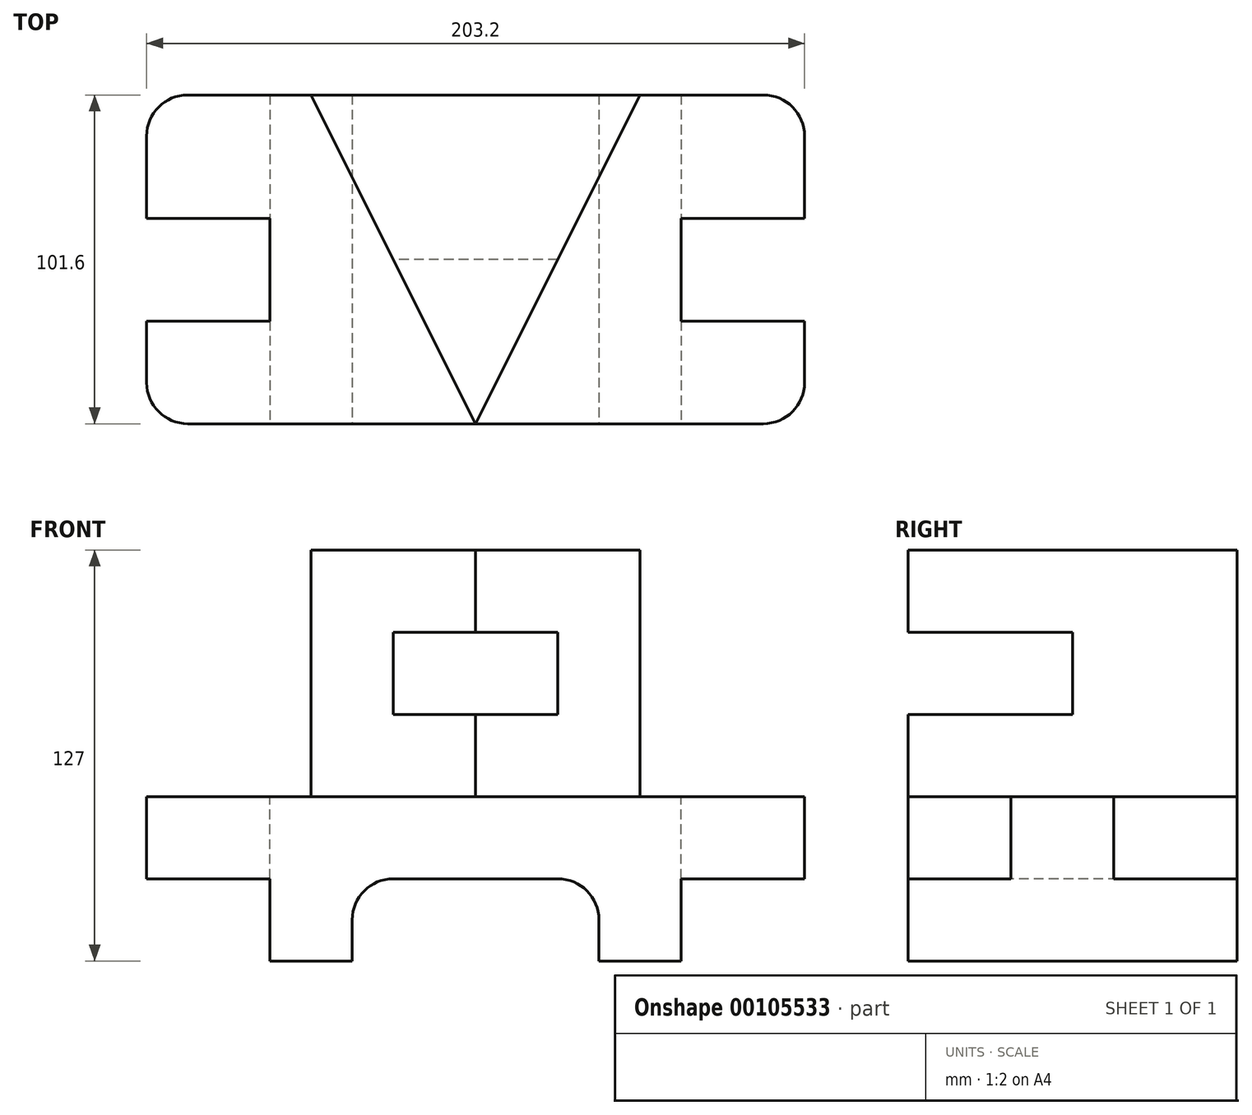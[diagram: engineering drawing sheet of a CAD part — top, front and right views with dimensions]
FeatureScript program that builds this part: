
annotation { "Feature Type Name" : "Feature", "Feature Type Description" : "" }
export const myFeature = defineFeature(function(context is Context, id is Id, definition is map)
    precondition{}
    {
        {
            var Q0;
            Q0=qCreatedBy(makeId("Front.planeOp"),FACE);
            var sketch = newSketch(context, id + "F0", { "sketchPlane" : qUnion([Q0])});
            skLineSegment(sketch, "E0", {"start": v(0, 0) * mm, "end": v(0, 25.4) * mm, "construction": true});
            skLineSegment(sketch, "E1", {"start": v(0, 0) * mm, "end": v(-38.1, 0) * mm, "construction": true});
            skLineSegment(sketch, "E2", {"start": v(-38.1, 0) * mm, "end": v(-38.1, 12.7) * mm});
            skLineSegment(sketch, "E3", {"start": v(0, 25.4) * mm, "end": v(-25.4, 25.4) * mm});
            skArc(sketch, "E4", {"start": v(-25.4, 25.4) * mm, "mid": v(-34.38, 21.68) * mm, "end": v(-38.1, 12.7) * mm});
            skLineSegment(sketch, "E5", {"start": v(-38.1, 0) * mm, "end": v(-63.5, 0) * mm});
            skLineSegment(sketch, "E6", {"start": v(-63.5, 0) * mm, "end": v(-63.5, 25.4) * mm});
            skLineSegment(sketch, "E7", {"start": v(-63.5, 25.4) * mm, "end": v(-101.6, 25.4) * mm});
            skLineSegment(sketch, "E8", {"start": v(-101.6, 25.4) * mm, "end": v(-101.6, 50.8) * mm});
            skLineSegment(sketch, "E9", {"start": v(-101.6, 50.8) * mm, "end": v(0, 50.8) * mm});
            skLineSegment(sketch, "E10.MirrorCS", {"start": v(101.6, 50.8) * mm, "end": v(0, 50.8) * mm});
            skLineSegment(sketch, "E11.MirrorCS", {"start": v(0, 0) * mm, "end": v(38.1, 0) * mm, "construction": true});
            skLineSegment(sketch, "E12.MirrorCS", {"start": v(38.1, 0) * mm, "end": v(38.1, 12.7) * mm});
            skLineSegment(sketch, "E13.MirrorCS", {"start": v(38.1, 0) * mm, "end": v(63.5, 0) * mm});
            skLineSegment(sketch, "E14.MirrorCS", {"start": v(63.5, 25.4) * mm, "end": v(101.6, 25.4) * mm});
            skArc(sketch, "E15.MirrorCS", {"start": v(25.4, 25.4) * mm, "mid": v(34.38, 21.68) * mm, "end": v(38.1, 12.7) * mm});
            skLineSegment(sketch, "E16.MirrorCS", {"start": v(0, 25.4) * mm, "end": v(25.4, 25.4) * mm});
            skLineSegment(sketch, "E17.MirrorCS", {"start": v(63.5, 0) * mm, "end": v(63.5, 25.4) * mm});
            skLineSegment(sketch, "E18.MirrorCS", {"start": v(101.6, 25.4) * mm, "end": v(101.6, 50.8) * mm});
            skSolve(sketch);
        }
        {
            var Q0;
            Q0 = qSketchRegion(id + "F0", true);
            extrude(context, id + "F1", {"entities" : qUnion([Q0]), "oppositeDirection" : true, "depth" : 101.6 * mm});
        }
        {
            var Q0;
            Q0=makeQuery(id+"F1.opExtrude","SWEPT_FACE",FACE,{"disambiguationData":[OSD([sQuery(id+"F0.wireOp",EDGE,"E9"),sQuery(id+"F0.wireOp",EDGE,"E10.MirrorCS")])]});
            var sketch = newSketch(context, id + "F2", { "sketchPlane" : qUnion([Q0])});
            skLineSegment(sketch, "E19", {"start": v(0, 0) * mm, "end": v(-63.5, 0) * mm, "construction": true});
            skLineSegment(sketch, "E20", {"start": v(-63.5, 0) * mm, "end": v(-63.5, 31.75) * mm, "construction": true});
            skLineSegment(sketch, "E21", {"start": v(-63.5, 31.75) * mm, "end": v(-63.5, 63.5) * mm, "construction": true});
            skLineSegment(sketch, "E22", {"start": v(-63.5, 31.75) * mm, "end": v(-101.6, 31.75) * mm});
            skLineSegment(sketch, "E23", {"start": v(-63.5, 31.75) * mm, "end": v(-63.5, 63.5) * mm});
            skLineSegment(sketch, "E24", {"start": v(-63.5, 63.5) * mm, "end": v(-101.6, 63.5) * mm});
            skLineSegment(sketch, "E25", {"start": v(-101.6, 63.5) * mm, "end": v(-101.6, 31.75) * mm});
            skLineSegment(sketch, "E26.MirrorCS", {"start": v(63.5, 31.75) * mm, "end": v(63.5, 63.5) * mm, "construction": true});
            skLineSegment(sketch, "E27.MirrorCS", {"start": v(63.5, 63.5) * mm, "end": v(101.6, 63.5) * mm});
            skLineSegment(sketch, "E28.MirrorCS", {"start": v(63.5, 31.75) * mm, "end": v(101.6, 31.75) * mm});
            skLineSegment(sketch, "E29.MirrorCS", {"start": v(101.6, 63.5) * mm, "end": v(101.6, 31.75) * mm});
            skLineSegment(sketch, "E30", {"start": v(63.5, 63.5) * mm, "end": v(63.5, 31.75) * mm});
            skSolve(sketch);
        }
        {
            var Q0;
            Q0=makeQuery(id+"F2.imprint","IMPRINT",FACE,{"disambiguationData":[TD([[makeQuery(id+"F2.imprint","IMPRINT",EDGE,{"derivedFrom":sQuery(id+"F2.wireOp",EDGE,"E27.MirrorCS")}),-1.0]])]});
            var Q1;
            Q1=makeQuery(id+"F2.imprint","IMPRINT",FACE,{"disambiguationData":[TD([[makeQuery(id+"F2.imprint","IMPRINT",EDGE,{"derivedFrom":sQuery(id+"F2.wireOp",EDGE,"E22")}),-1.0]])]});
            extrude(context, id + "F3", {"entities" : qUnion([Q0, Q1]), "operationType" : NewBodyOperationType.REMOVE, "oppositeDirection" : true, "depth" : 25.4 * mm});
        }
        {
            var Q0;
            Q0=makeQuery(id+"F1.opExtrude","SWEPT_FACE",FACE,{"disambiguationData":[OSD([sQuery(id+"F0.wireOp",EDGE,"E9"),sQuery(id+"F0.wireOp",EDGE,"E10.MirrorCS")])]});
            var sketch = newSketch(context, id + "F4", { "sketchPlane" : qUnion([Q0])});
            skLineSegment(sketch, "E31", {"start": v(0, 0) * mm, "end": v(0, 101.6) * mm, "construction": true});
            skLineSegment(sketch, "E32", {"start": v(0, 101.6) * mm, "end": v(-50.8, 101.6) * mm, "construction": true});
            skLineSegment(sketch, "E33", {"start": v(0, 101.6) * mm, "end": v(50.8, 101.6) * mm, "construction": true});
            skLineSegment(sketch, "E34", {"start": v(-50.8, 101.6) * mm, "end": v(50.8, 101.6) * mm});
            skLineSegment(sketch, "E35", {"start": v(-50.8, 101.6) * mm, "end": v(0, 0) * mm});
            skLineSegment(sketch, "E36", {"start": v(0, 0) * mm, "end": v(50.8, 101.6) * mm});
            skSolve(sketch);
        }
        {
            var Q0;
            Q0 = qSketchRegion(id + "F4", true);
            extrude(context, id + "F5", {"entities" : qUnion([Q0]), "operationType" : NewBodyOperationType.ADD, "depth" : 76.2 * mm});
        }
        {
            var Q0;
            Q0=qCreatedBy(makeId("Front.planeOp"),FACE);
            var sketch = newSketch(context, id + "F6", { "sketchPlane" : qUnion([Q0])});
            skLineSegment(sketch, "E37", {"start": v(0, 0) * mm, "end": v(0, 76.2) * mm, "construction": true});
            skLineSegment(sketch, "E38", {"start": v(0, 76.2) * mm, "end": v(-50.8, 76.2) * mm});
            skLineSegment(sketch, "E39", {"start": v(-50.8, 76.2) * mm, "end": v(-50.8, 101.6) * mm});
            skLineSegment(sketch, "E40", {"start": v(0, 76.2) * mm, "end": v(50.8, 76.2) * mm});
            skLineSegment(sketch, "E41", {"start": v(50.8, 76.2) * mm, "end": v(50.8, 101.6) * mm});
            skLineSegment(sketch, "E42", {"start": v(50.8, 101.6) * mm, "end": v(-50.8, 101.6) * mm});
            skSolve(sketch);
        }
        {
            var Q0;
            Q0=makeQuery(id+"F6.imprint","IMPRINT",FACE,{"disambiguationData":[TD([[makeQuery(id+"F6.imprint","IMPRINT",EDGE,{"derivedFrom":sQuery(id+"F6.wireOp",EDGE,"E38")}),-1.0]])]});
            extrude(context, id + "F7", {"entities" : qUnion([Q0]), "operationType" : NewBodyOperationType.REMOVE, "oppositeDirection" : true, "depth" : 50.8 * mm});
        }
        {
            var Q0;
            Q0=qCreatedBy(makeId("Top.planeOp"),FACE);
            var sketch = newSketch(context, id + "F8", { "sketchPlane" : qUnion([Q0])});
            skLineSegment(sketch, "E43", {"start": v(0, 0) * mm, "end": v(-88.9, 0) * mm, "construction": true});
            skLineSegment(sketch, "E44", {"start": v(-88.9, 0) * mm, "end": v(-88.9, 12.7) * mm, "construction": true});
            skLineSegment(sketch, "E45", {"start": v(-88.9, 12.7) * mm, "end": v(-101.6, 12.7) * mm, "construction": true});
            skLineSegment(sketch, "E46", {"start": v(-101.6, 12.7) * mm, "end": v(-101.6, 88.9) * mm, "construction": true});
            skLineSegment(sketch, "E47", {"start": v(-101.6, 88.9) * mm, "end": v(-88.9, 88.9) * mm, "construction": true});
            skLineSegment(sketch, "E48", {"start": v(-88.9, 88.9) * mm, "end": v(-88.9, 101.6) * mm, "construction": true});
            skLineSegment(sketch, "E49", {"start": v(-88.9, 101.6) * mm, "end": v(0, 101.6) * mm, "construction": true});
            skLineSegment(sketch, "E50", {"start": v(-88.9, 101.6) * mm, "end": v(0, 101.6) * mm});
            skLineSegment(sketch, "E51", {"start": v(0, 101.6) * mm, "end": v(0, 0) * mm});
            skLineSegment(sketch, "E52", {"start": v(0, 0) * mm, "end": v(-88.9, 0) * mm});
            skLineSegment(sketch, "E53", {"start": v(-101.6, 12.7) * mm, "end": v(-101.6, 88.9) * mm});
            skArc(sketch, "E54", {"start": v(-88.9, 101.6) * mm, "mid": v(-97.88, 97.88) * mm, "end": v(-101.6, 88.9) * mm});
            skArc(sketch, "E55", {"start": v(-101.6, 12.7) * mm, "mid": v(-97.88, 3.72) * mm, "end": v(-88.9, 0) * mm});
            skLineSegment(sketch, "E56.MirrorCS", {"start": v(88.9, 101.6) * mm, "end": v(0, 101.6) * mm});
            skLineSegment(sketch, "E57.MirrorCS", {"start": v(0, 0) * mm, "end": v(88.9, 0) * mm});
            skLineSegment(sketch, "E58.MirrorCS", {"start": v(101.6, 12.7) * mm, "end": v(101.6, 88.9) * mm});
            skArc(sketch, "E59.MirrorCS", {"start": v(88.9, 101.6) * mm, "mid": v(97.88, 97.88) * mm, "end": v(101.6, 88.9) * mm});
            skLineSegment(sketch, "E60.MirrorCS", {"start": v(88.9, 101.6) * mm, "end": v(0, 101.6) * mm, "construction": true});
            skLineSegment(sketch, "E61.MirrorCS", {"start": v(88.9, 88.9) * mm, "end": v(88.9, 101.6) * mm, "construction": true});
            skLineSegment(sketch, "E62.MirrorCS", {"start": v(88.9, 12.7) * mm, "end": v(101.6, 12.7) * mm, "construction": true});
            skArc(sketch, "E63.MirrorCS", {"start": v(101.6, 12.7) * mm, "mid": v(97.88, 3.72) * mm, "end": v(88.9, 0) * mm});
            skLineSegment(sketch, "E64.MirrorCS", {"start": v(0, 0) * mm, "end": v(88.9, 0) * mm, "construction": true});
            skLineSegment(sketch, "E65.MirrorCS", {"start": v(101.6, 12.7) * mm, "end": v(101.6, 88.9) * mm, "construction": true});
            skLineSegment(sketch, "E66.MirrorCS", {"start": v(101.6, 88.9) * mm, "end": v(88.9, 88.9) * mm, "construction": true});
            skLineSegment(sketch, "E67.MirrorCS", {"start": v(88.9, 0) * mm, "end": v(88.9, 12.7) * mm, "construction": true});
            skSolve(sketch);
        }
        {
            var Q0;
            Q0 = qSketchRegion(id + "F8", true);
            extrude(context, id + "F9", {"entities" : qUnion([Q0]), "operationType" : NewBodyOperationType.INTERSECT, "endBound" : BoundingType.SYMMETRIC, "depth" : 254 * mm});
        }
    });
